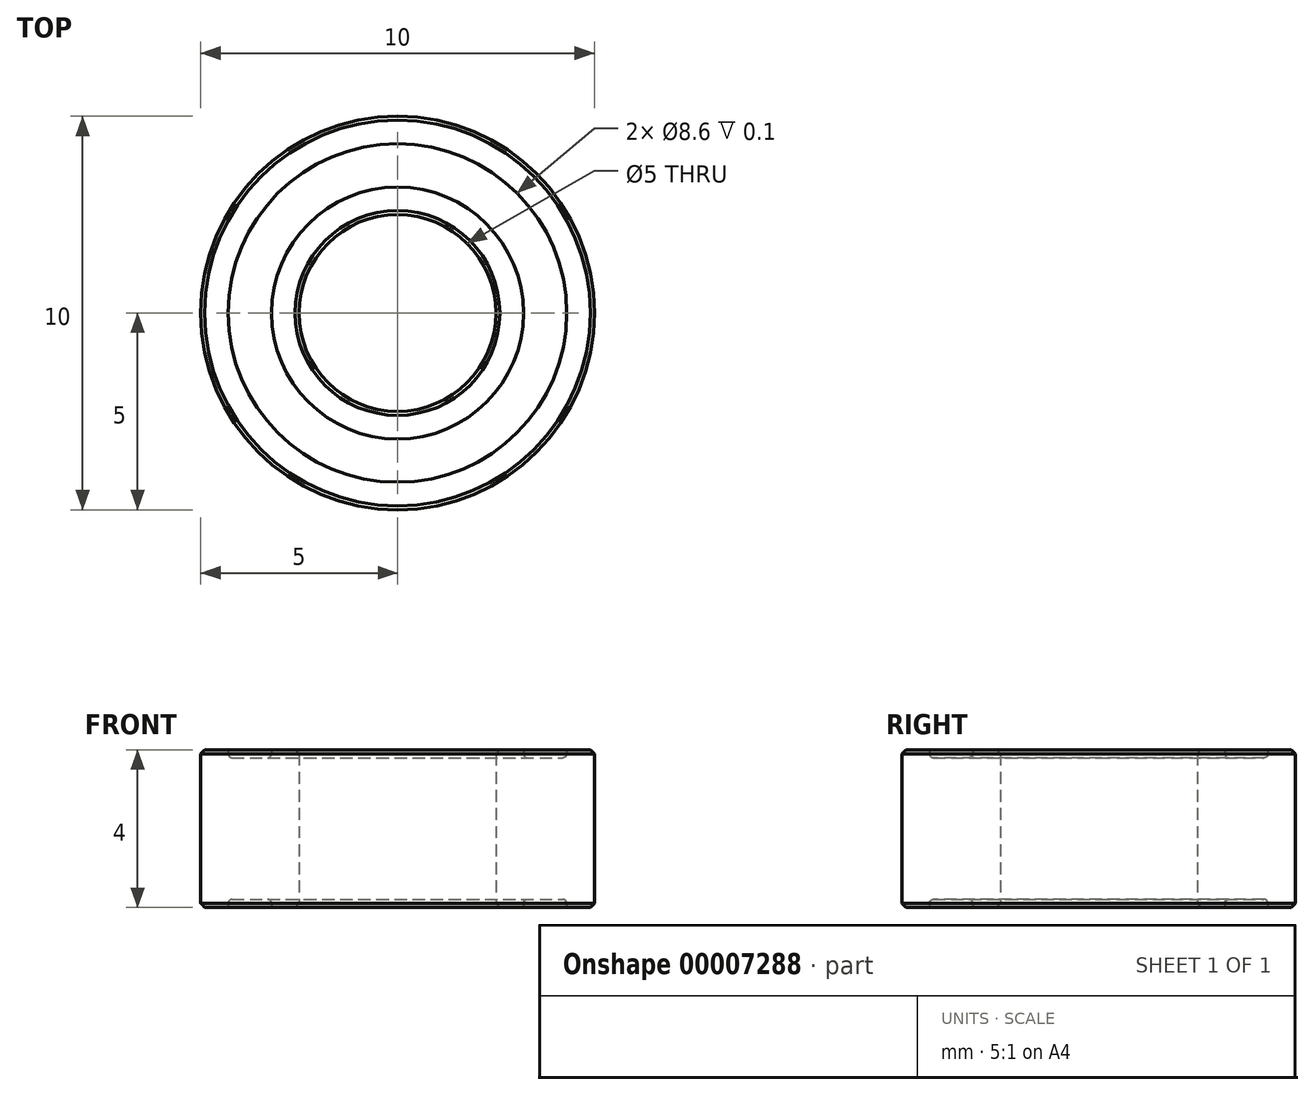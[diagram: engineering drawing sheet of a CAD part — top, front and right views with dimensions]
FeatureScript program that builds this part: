
annotation { "Feature Type Name" : "Feature", "Feature Type Description" : "" }
export const myFeature = defineFeature(function(context is Context, id is Id, definition is map)
    precondition{}
    {
        {
            var Q0;
            Q0=qCreatedBy(makeId("Front.planeOp"),FACE);
            var sketch = newSketch(context, id + "F0", { "sketchPlane" : qUnion([Q0])});
            skLineSegment(sketch, "E0", {"start": v(0, 0) * mm, "end": v(2.5, 0) * mm, "construction": true});
            skLineSegment(sketch, "E1", {"start": v(2.5, 0) * mm, "end": v(5, 0) * mm, "construction": true});
            skLineSegment(sketch, "E2", {"start": v(0, 0) * mm, "end": v(-2.5, 0) * mm, "construction": true});
            skLineSegment(sketch, "E3", {"start": v(-2.5, 0) * mm, "end": v(-5, 0) * mm, "construction": true});
            skLineSegment(sketch, "E4", {"start": v(0, 0) * mm, "end": v(0, 6.94) * mm, "construction": true});
            skLineSegment(sketch, "E5", {"start": v(2.5, 0) * mm, "end": v(2.5, 2) * mm});
            skLineSegment(sketch, "E6", {"start": v(2.5, 2) * mm, "end": v(3.2, 2) * mm});
            skLineSegment(sketch, "E7", {"start": v(3.2, 2) * mm, "end": v(3.2, 1.8) * mm});
            skLineSegment(sketch, "E8", {"start": v(3.2, 1.8) * mm, "end": v(4.3, 1.8) * mm});
            skLineSegment(sketch, "E9", {"start": v(4.3, 1.8) * mm, "end": v(4.3, 2) * mm});
            skLineSegment(sketch, "E10", {"start": v(4.3, 2) * mm, "end": v(5, 2) * mm});
            skLineSegment(sketch, "E11", {"start": v(5, 2) * mm, "end": v(5, 0) * mm});
            skLineSegment(sketch, "E12.0.MirrorCS", {"start": v(5, -2) * mm, "end": v(5, 0) * mm});
            skLineSegment(sketch, "E12.1.MirrorCS", {"start": v(4.3, -1.8) * mm, "end": v(4.3, -2) * mm});
            skLineSegment(sketch, "E12.2.MirrorCS", {"start": v(2.5, 0) * mm, "end": v(2.5, -2) * mm});
            skLineSegment(sketch, "E12.3.MirrorCS", {"start": v(3.2, -1.8) * mm, "end": v(4.3, -1.8) * mm});
            skLineSegment(sketch, "E12.4.MirrorCS", {"start": v(2.5, -2) * mm, "end": v(3.2, -2) * mm});
            skLineSegment(sketch, "E12.5.MirrorCS", {"start": v(4.3, -2) * mm, "end": v(5, -2) * mm});
            skLineSegment(sketch, "E12.6.MirrorCS", {"start": v(3.2, -2) * mm, "end": v(3.2, -1.8) * mm});
            skSolve(sketch);
        }
        {
            var Q0;
            Q0 = qSketchRegion(id + "F0", true);
            var Q1;
            Q1=sQuery(id+"F0.wireOp",EDGE,"E4");
            revolve(context, id + "F1", {"entities" : qUnion([Q0]), "axis" : qUnion([Q1]), "revolveType" : RevolveType.FULL});
        }
        {
            var Q0;
            Q0=makeQuery(id+"F1.opRevolve","SWEPT_EDGE",EDGE,{"disambiguationData":[OSD([sQuery(id+"F0.wireOp",EDGE,"E10"),sQuery(id+"F0.wireOp",EDGE,"E11")])]});
            var Q1;
            Q1=makeQuery(id+"F1.opRevolve","SWEPT_EDGE",EDGE,{"disambiguationData":[OSD([sQuery(id+"F0.wireOp",EDGE,"E12.0.MirrorCS"),sQuery(id+"F0.wireOp",EDGE,"E12.5.MirrorCS")])]});
            var Q2;
            Q2=makeQuery(id+"F1.opRevolve","SWEPT_EDGE",EDGE,{"disambiguationData":[OSD([sQuery(id+"F0.wireOp",EDGE,"E5"),sQuery(id+"F0.wireOp",EDGE,"E6")])]});
            var Q3;
            Q3=makeQuery(id+"F1.opRevolve","SWEPT_EDGE",EDGE,{"disambiguationData":[OSD([sQuery(id+"F0.wireOp",EDGE,"E12.2.MirrorCS"),sQuery(id+"F0.wireOp",EDGE,"E12.4.MirrorCS")])]});
            chamfer(context, id + "F2", {"entities" : qUnion([Q0, Q1, Q2, Q3]), "width" : .1 * mm, "tangentPropagation" : true});
        }
        {
            var Q0;
            Q0=makeQuery(id+"F1.opRevolve","SWEPT_EDGE",EDGE,{"disambiguationData":[OSD([sQuery(id+"F0.wireOp",EDGE,"E8"),sQuery(id+"F0.wireOp",EDGE,"E9")])]});
            var Q1;
            Q1=makeQuery(id+"F1.opRevolve","SWEPT_EDGE",EDGE,{"disambiguationData":[OSD([sQuery(id+"F0.wireOp",EDGE,"E7"),sQuery(id+"F0.wireOp",EDGE,"E8")])]});
            var Q2;
            Q2=makeQuery(id+"F1.opRevolve","SWEPT_EDGE",EDGE,{"disambiguationData":[OSD([sQuery(id+"F0.wireOp",EDGE,"E12.3.MirrorCS"),sQuery(id+"F0.wireOp",EDGE,"E12.6.MirrorCS")])]});
            var Q3;
            Q3=makeQuery(id+"F1.opRevolve","SWEPT_EDGE",EDGE,{"disambiguationData":[OSD([sQuery(id+"F0.wireOp",EDGE,"E12.1.MirrorCS"),sQuery(id+"F0.wireOp",EDGE,"E12.3.MirrorCS")])]});
            fillet(context, id + "F3", {"entities" : qUnion([Q0, Q1, Q2, Q3]), "radius" : .1 * mm, "tangentPropagation" : true, "allowEdgeOverflow" : false});
        }
    });
